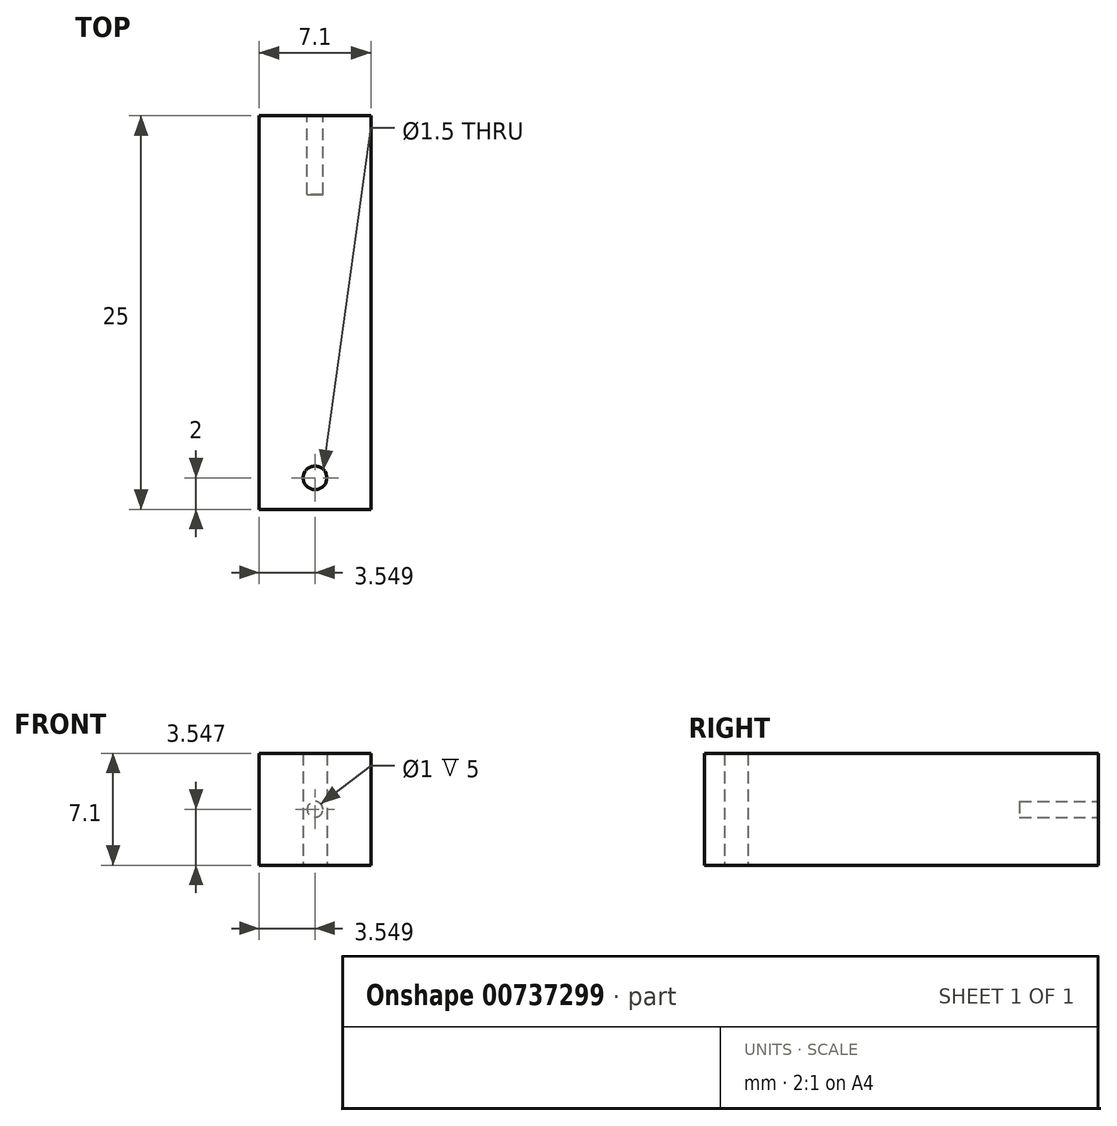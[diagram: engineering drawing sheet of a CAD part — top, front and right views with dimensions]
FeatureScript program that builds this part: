
annotation { "Feature Type Name" : "Feature", "Feature Type Description" : "" }
export const myFeature = defineFeature(function(context is Context, id is Id, definition is map)
    precondition{}
    {
        {
            var Q0;
            Q0=qCreatedBy(makeId("Front.planeOp"),FACE);
            var sketch = newSketch(context, id + "F0", { "sketchPlane" : qUnion([Q0])});
            skLineSegment(sketch, "E0.bottom", {"start": v(18.82, -17.4) * mm, "end": v(25.92, -17.4) * mm});
            skLineSegment(sketch, "E0.top", {"start": v(18.82, -24.5) * mm, "end": v(25.92, -24.5) * mm});
            skLineSegment(sketch, "E0.left", {"start": v(18.82, -17.4) * mm, "end": v(18.82, -24.5) * mm});
            skLineSegment(sketch, "E0.right", {"start": v(25.92, -17.4) * mm, "end": v(25.92, -24.5) * mm});
            skSolve(sketch);
        }
        {
            var Q0;
            Q0 = qSketchRegion(id + "F0", true);
            extrude(context, id + "F1", {"entities" : qUnion([Q0]), "depth" : 25 * mm, "offsetDistance" : 25 * mm});
        }
        {
            var Q0;
            Q0=makeQuery(id+"F1.opExtrude","SWEPT_FACE",FACE,{"disambiguationData":[OSD([sQuery(id+"F0.wireOp",EDGE,"E0.top")])]});
            var sketch = newSketch(context, id + "F2", { "sketchPlane" : qUnion([Q0])});
            skCircle(sketch, "E1", {"center": v(22.37, 23) * mm, "radius": 0.75 * mm});
            skPoint(sketch, "E1.centerSnap0", {"position": v(22.37, 25) * mm});
            skSolve(sketch);
        }
        {
            var Q0;
            Q0 = qSketchRegion(id + "F2", true);
            extrude(context, id + "F3", {"entities" : qUnion([Q0]), "operationType" : NewBodyOperationType.REMOVE, "oppositeDirection" : true, "depth" : 25 * mm, "offsetDistance" : 25 * mm});
        }
        {
            var Q0;
            Q0=makeQuery(id+"F1.opExtrude","CAP_FACE",FACE,{"disambiguationData":[OSD([sQuery(id+"F0.wireOp",EDGE,"E0.bottom"),sQuery(id+"F0.wireOp",EDGE,"E0.top"),sQuery(id+"F0.wireOp",EDGE,"E0.left"),sQuery(id+"F0.wireOp",EDGE,"E0.right")])],"isStart":true});
            var sketch = newSketch(context, id + "F4", { "sketchPlane" : qUnion([Q0])});
            skCircle(sketch, "E2", {"center": v(-22.37, -20.95) * mm, "radius": 0.5 * mm});
            skSolve(sketch);
        }
        {
            var Q0;
            Q0 = qSketchRegion(id + "F4", true);
            extrude(context, id + "F5", {"entities" : qUnion([Q0]), "operationType" : NewBodyOperationType.REMOVE, "oppositeDirection" : true, "depth" : 5 * mm, "offsetDistance" : 25 * mm});
        }
    });
